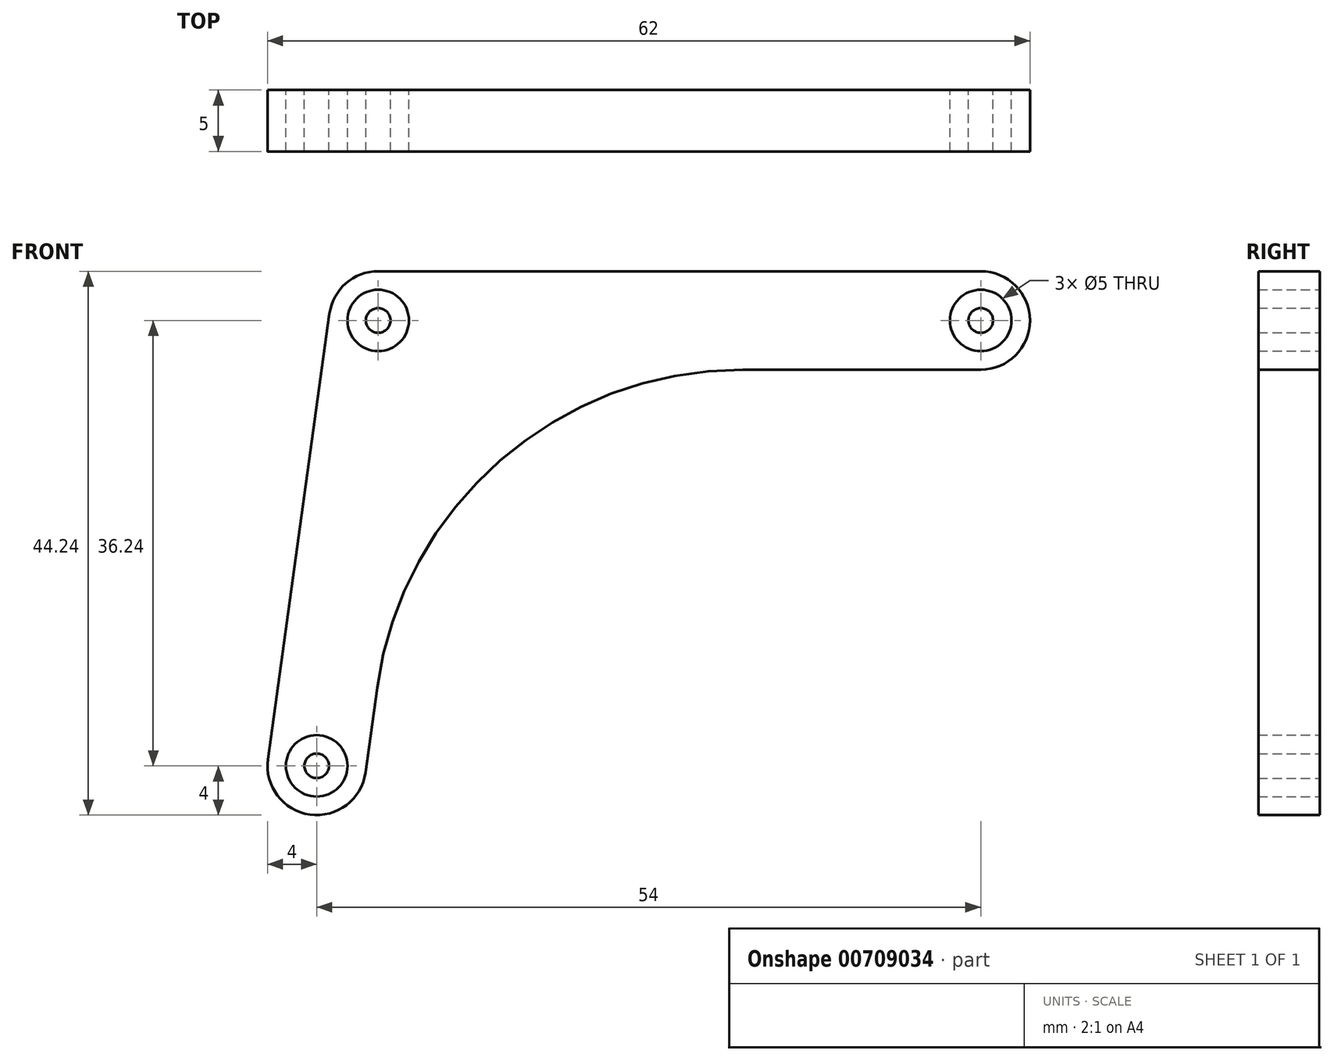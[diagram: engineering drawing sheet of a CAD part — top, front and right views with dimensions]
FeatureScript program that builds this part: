
annotation { "Feature Type Name" : "Feature", "Feature Type Description" : "" }
export const myFeature = defineFeature(function(context is Context, id is Id, definition is map)
    precondition{}
    {
        {
            var Q0;
            Q0=qCreatedBy(makeId("Front.planeOp"),FACE);
            var sketch = newSketch(context, id + "F0", { "sketchPlane" : qUnion([Q0])});
            skArc(sketch, "E0", {"start": v(0, 4) * mm, "mid": v(-2.63, 3.02) * mm, "end": v(-3.96, 0.55) * mm});
            skCircle(sketch, "E1", {"center": v(0, 0) * mm, "radius": 2.5 * mm});
            skCircle(sketch, "E2", {"center": v(0, 0) * mm, "radius": 1 * mm});
            skArc(sketch, "E3", {"start": v(-8.96, -35.7) * mm, "mid": v(-5.55, -40.2) * mm, "end": v(-1.04, -36.79) * mm});
            skCircle(sketch, "E4", {"center": v(-5, -36.24) * mm, "radius": 2.5 * mm});
            skCircle(sketch, "E5", {"center": v(-5, -36.24) * mm, "radius": 1 * mm});
            skCircle(sketch, "E6", {"center": v(49, 0) * mm, "radius": 1 * mm});
            skArc(sketch, "E7", {"start": v(49, -4) * mm, "mid": v(53, 0) * mm, "end": v(49, 4) * mm});
            skCircle(sketch, "E8", {"center": v(49, 0) * mm, "radius": 2.5 * mm});
            skLineSegment(sketch, "E9", {"start": v(-3.96, 0.55) * mm, "end": v(-8.96, -35.7) * mm});
            skLineSegment(sketch, "E10", {"start": v(-0.09, -29.9) * mm, "end": v(-1.04, -36.79) * mm});
            skLineSegment(sketch, "E11", {"start": v(0, 4) * mm, "end": v(49, 4) * mm});
            skLineSegment(sketch, "E12", {"start": v(29.63, -4) * mm, "end": v(49, -4) * mm});
            skPoint(sketch, "E13.visualSharp", {"position": v(3.49, -4) * mm});
            skArc(sketch, "E13.filletArc", {"start": v(29.63, -4) * mm, "mid": v(9.92, -11.38) * mm, "end": v(-0.09, -29.9) * mm});
            skSolve(sketch);
        }
        {
            var Q0;
            Q0=makeQuery(id+"F0.imprint","IMPRINT",FACE,{"disambiguationData":[TD([[makeQuery(id+"F0.imprint","IMPRINT",EDGE,{"derivedFrom":sQuery(id+"F0.wireOp",EDGE,"E0")}),1.0]])]});
            var Q1;
            Q1=makeQuery(id+"F0.imprint","IMPRINT",FACE,{"disambiguationData":[TD([[makeQuery(id+"F0.imprint","IMPRINT",EDGE,{"derivedFrom":sQuery(id+"F0.wireOp",EDGE,"E5")}),1.0]])]});
            var Q2;
            Q2=makeQuery(id+"F0.imprint","IMPRINT",FACE,{"disambiguationData":[TD([[makeQuery(id+"F0.imprint","IMPRINT",EDGE,{"derivedFrom":sQuery(id+"F0.wireOp",EDGE,"E6")}),1.0]])]});
            var Q3;
            Q3=makeQuery(id+"F0.imprint","IMPRINT",FACE,{"disambiguationData":[TD([[makeQuery(id+"F0.imprint","IMPRINT",EDGE,{"derivedFrom":sQuery(id+"F0.wireOp",EDGE,"E2")}),1.0]])]});
            extrude(context, id + "F1", {"entities" : qUnion([Q0, Q1, Q2, Q3]), "depth" : 5 * mm, "offsetDistance" : 25 * mm});
        }
    });
